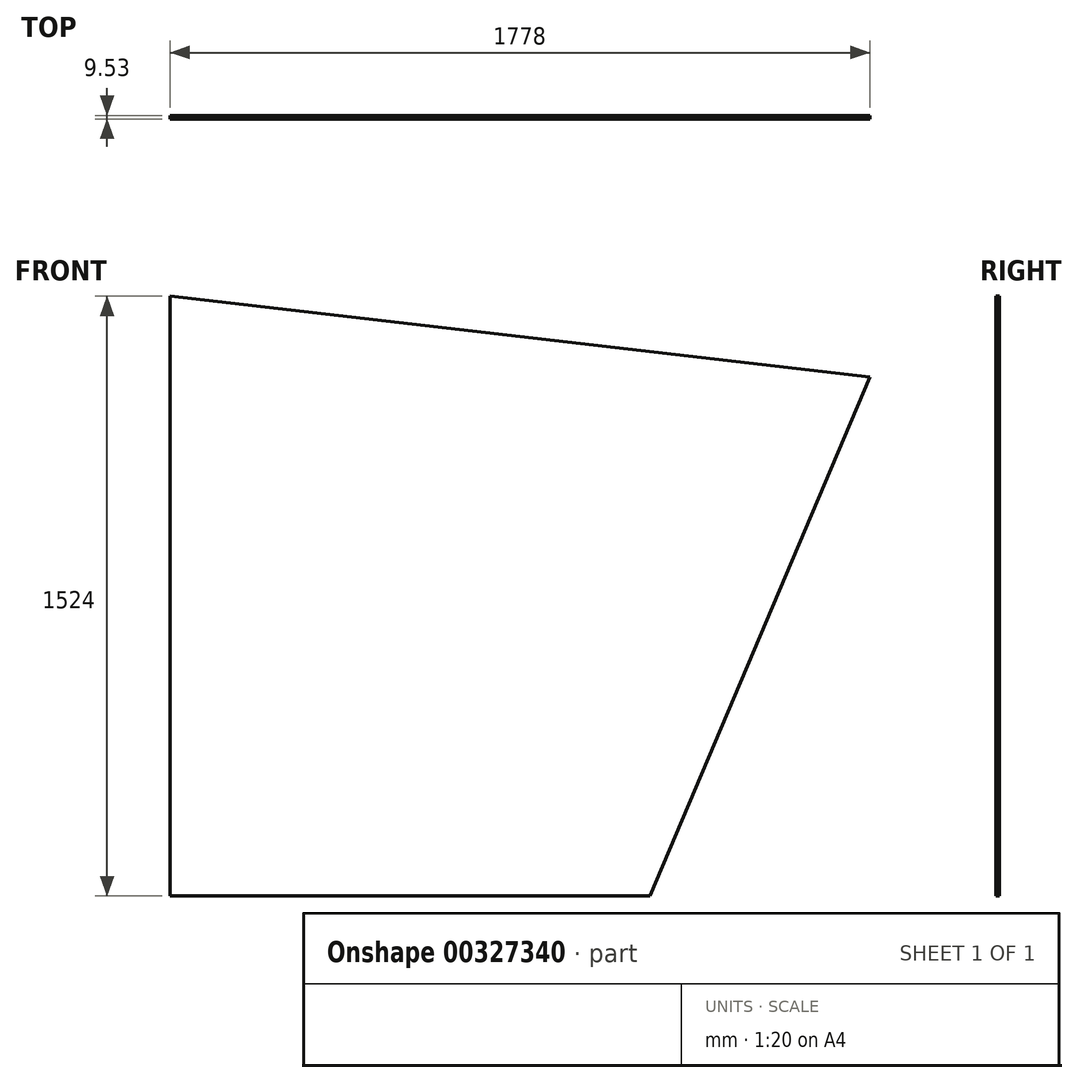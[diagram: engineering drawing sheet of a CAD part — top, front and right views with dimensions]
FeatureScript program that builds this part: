
annotation { "Feature Type Name" : "Feature", "Feature Type Description" : "" }
export const myFeature = defineFeature(function(context is Context, id is Id, definition is map)
    precondition{}
    {
        {
            var Q0;
            Q0=qCreatedBy(makeId("Front.planeOp"),FACE);
            var sketch = newSketch(context, id + "F0", { "sketchPlane" : qUnion([Q0])});
            skLineSegment(sketch, "E0", {"start": v(-904.16, 825.99) * mm, "end": v(873.84, 620.25) * mm});
            skLineSegment(sketch, "E1", {"start": v(873.84, 620.25) * mm, "end": v(315.04, -698.01) * mm});
            skLineSegment(sketch, "E2", {"start": v(315.04, -698.01) * mm, "end": v(-904.16, -698.01) * mm});
            skLineSegment(sketch, "E3", {"start": v(-904.16, -698.01) * mm, "end": v(-904.16, 825.99) * mm});
            skSolve(sketch);
        }
        {
            var Q0;
            Q0 = qSketchRegion(id + "F0", true);
            extrude(context, id + "F1", {"entities" : qUnion([Q0]), "depth" : 9.52 * mm});
        }
    });
